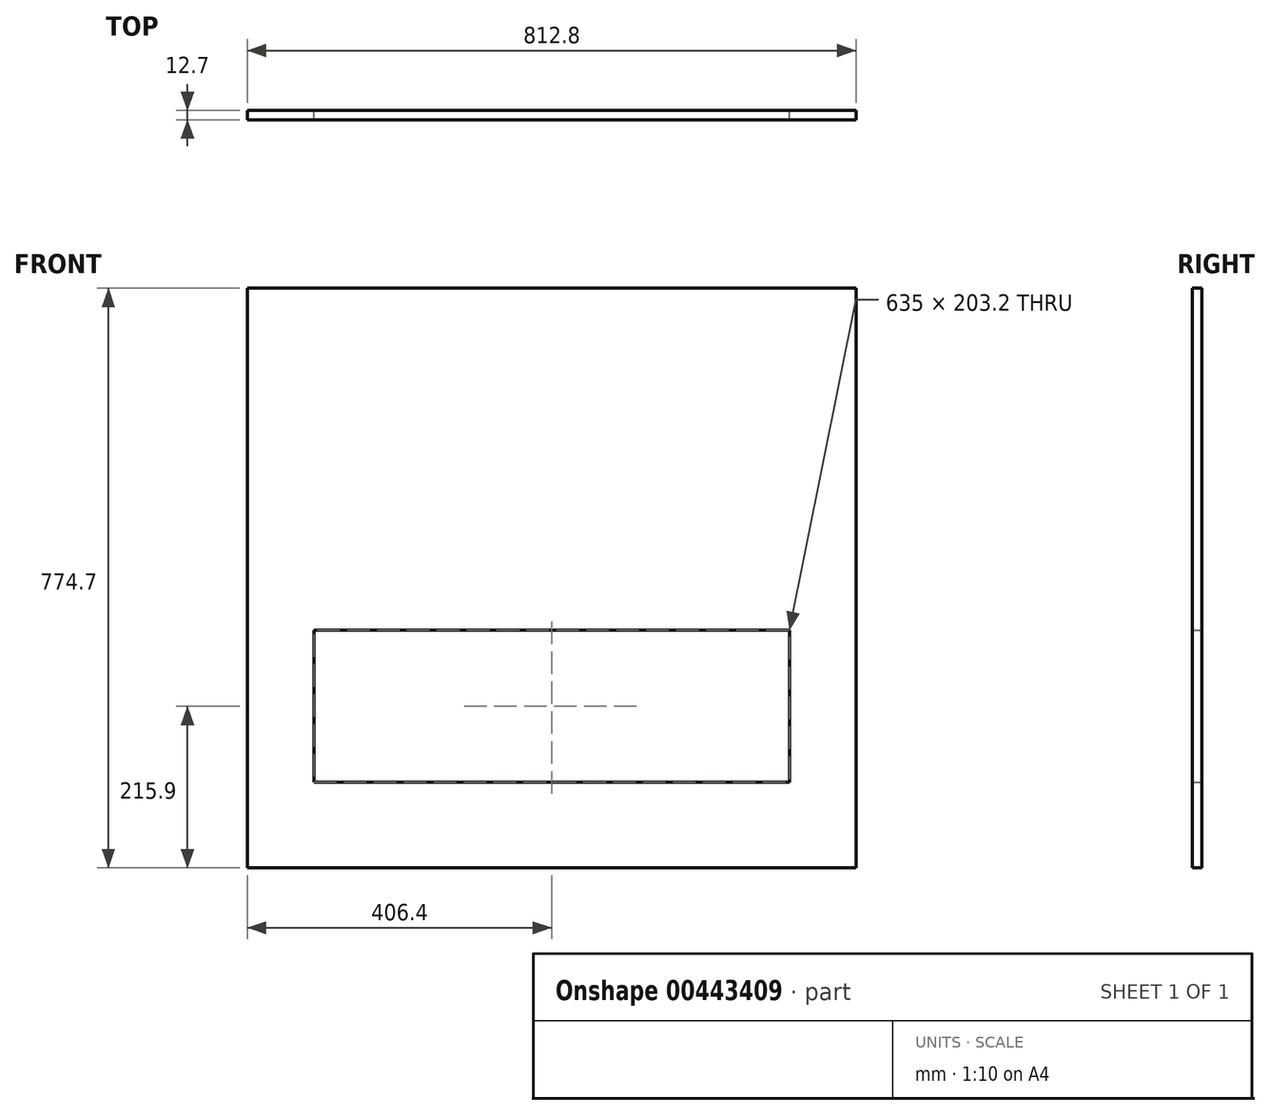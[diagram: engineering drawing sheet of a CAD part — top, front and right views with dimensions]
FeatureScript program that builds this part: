
annotation { "Feature Type Name" : "Feature", "Feature Type Description" : "" }
export const myFeature = defineFeature(function(context is Context, id is Id, definition is map)
    precondition{}
    {
        {
            var Q0;
            Q0=qCreatedBy(makeId("Front.planeOp"),FACE);
            var sketch = newSketch(context, id + "F0", { "sketchPlane" : qUnion([Q0])});
            skLineSegment(sketch, "E0.bottom", {"start": v(-406.4, 387.35) * mm, "end": v(406.4, 387.35) * mm});
            skLineSegment(sketch, "E0.top", {"start": v(-406.4, -387.35) * mm, "end": v(406.4, -387.35) * mm});
            skLineSegment(sketch, "E0.left", {"start": v(-406.4, 387.35) * mm, "end": v(-406.4, -387.35) * mm});
            skLineSegment(sketch, "E0.right", {"start": v(406.4, 387.35) * mm, "end": v(406.4, -387.35) * mm});
            skPoint(sketch, "E0.middle", {"position": v(0, 0) * mm});
            skLineSegment(sketch, "E1.bottom", {"start": v(317.5, -69.85) * mm, "end": v(-317.5, -69.85) * mm});
            skLineSegment(sketch, "E1.top", {"start": v(317.5, -273.05) * mm, "end": v(-317.5, -273.05) * mm});
            skLineSegment(sketch, "E1.left", {"start": v(317.5, -69.85) * mm, "end": v(317.5, -273.05) * mm});
            skLineSegment(sketch, "E1.right", {"start": v(-317.5, -69.85) * mm, "end": v(-317.5, -273.05) * mm});
            skPoint(sketch, "E1.middle", {"position": v(0, -171.45) * mm});
            skSolve(sketch);
        }
        {
            var Q0;
            Q0=makeQuery(id+"F0.imprint","IMPRINT",FACE,{"disambiguationData":[TD([[makeQuery(id+"F0.imprint","IMPRINT",EDGE,{"derivedFrom":sQuery(id+"F0.wireOp",EDGE,"E0.bottom")}),-1.0]])]});
            extrude(context, id + "F1", {"entities" : qUnion([Q0]), "depth" : 12.7 * mm});
        }
    });
